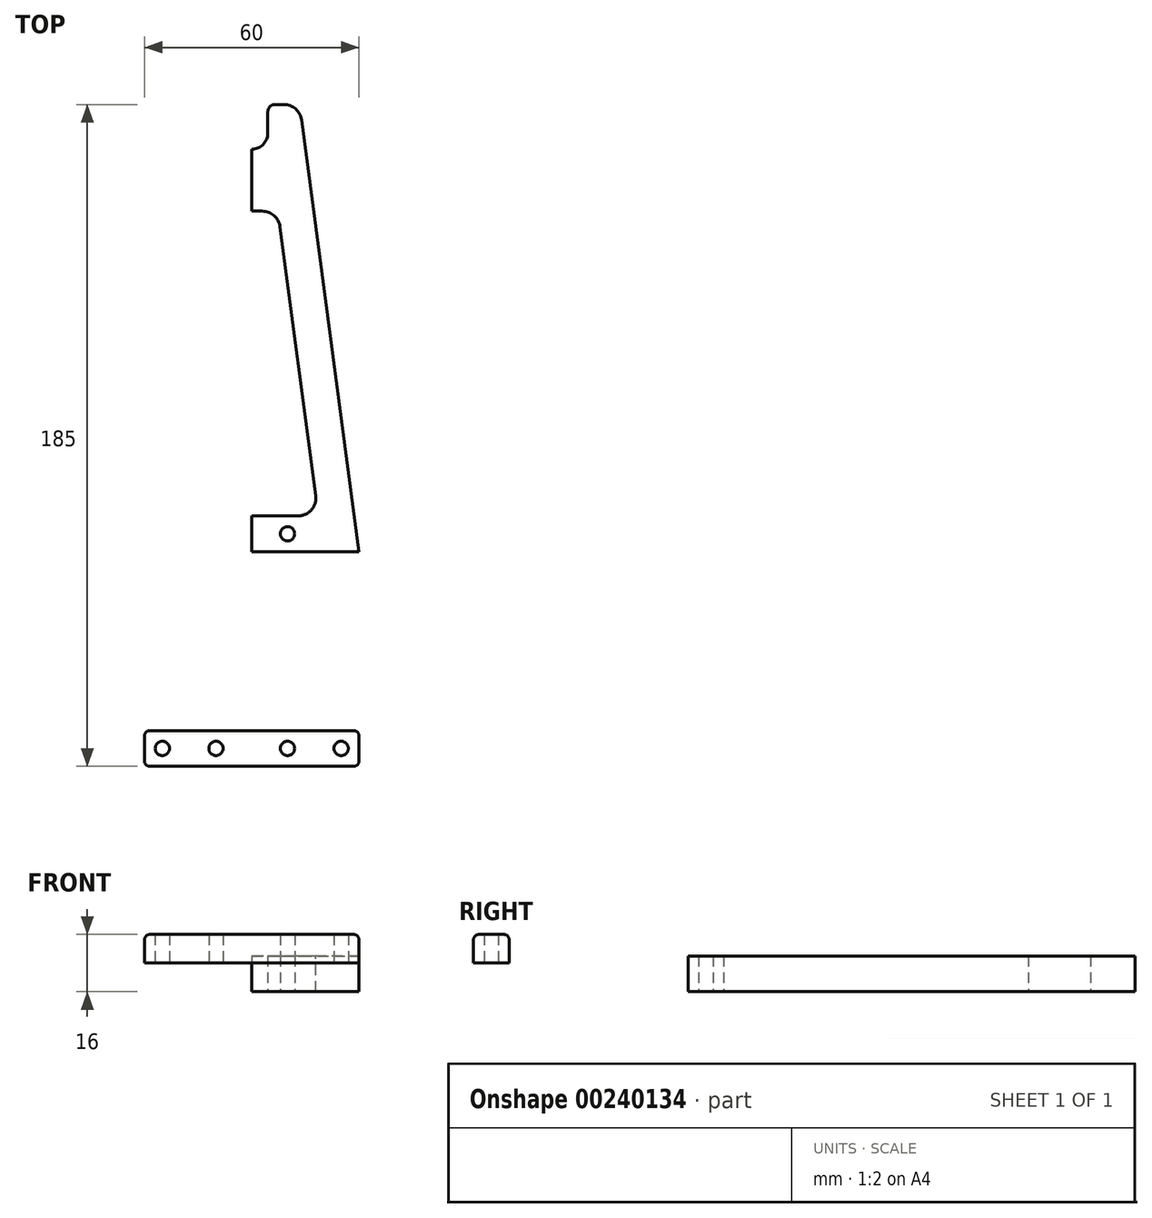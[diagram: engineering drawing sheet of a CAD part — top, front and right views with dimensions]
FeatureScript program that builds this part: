
annotation { "Feature Type Name" : "Feature", "Feature Type Description" : "" }
export const myFeature = defineFeature(function(context is Context, id is Id, definition is map)
    precondition{}
    {
        {
            var Q0;
            Q0=qCreatedBy(makeId("Top.planeOp"),FACE);
            var sketch = newSketch(context, id + "F0", { "sketchPlane" : qUnion([Q0])});
            skLineSegment(sketch, "E0.top", {"start": v(0, 75) * mm, "end": v(-30, 75) * mm});
            skPoint(sketch, "E0.middle", {"position": v(0, 0) * mm});
            skLineSegment(sketch, "E1", {"start": v(-30, 75) * mm, "end": v(-50, -75) * mm});
            skPoint(sketch, "E0.right.end.orphan", {"position": v(-50, 75) * mm});
            skPoint(sketch, "E0.left.end.orphan", {"position": v(50, 75) * mm});
            skLineSegment(sketch, "E2", {"start": v(0, 0) * mm, "end": v(0, 6) * mm});
            skLineSegment(sketch, "E3", {"start": v(-50, -75) * mm, "end": v(-40, -75) * mm});
            skLineSegment(sketch, "E4", {"start": v(-30, 75) * mm, "end": v(-20, 75) * mm});
            skLineSegment(sketch, "E5", {"start": v(0, 75) * mm, "end": v(0, 65) * mm});
            skLineSegment(sketch, "E6", {"start": v(0, 65) * mm, "end": v(-21.33, 65) * mm});
            skLineSegment(sketch, "E7", {"start": v(0, -75) * mm, "end": v(0, -65) * mm});
            skLineSegment(sketch, "E8", {"start": v(0, -65) * mm, "end": v(-38.67, -65) * mm});
            skLineSegment(sketch, "E9", {"start": v(0, 6) * mm, "end": v(-29.2, 6) * mm});
            skLineSegment(sketch, "E10", {"start": v(0, 0) * mm, "end": v(0, -6) * mm});
            skLineSegment(sketch, "E11", {"start": v(0, -6) * mm, "end": v(-30.8, -6) * mm});
            skLineSegment(sketch, "E12.trimOffspring", {"start": v(-30.8, -6) * mm, "end": v(-38.67, -65) * mm});
            skLineSegment(sketch, "E13", {"start": v(-21.33, 65) * mm, "end": v(-29.2, 6) * mm});
            skLineSegment(sketch, "E14.trimOffspring", {"start": v(0, -75) * mm, "end": v(-50, -75) * mm});
            skPoint(sketch, "E0.bottom.start.orphan", {"position": v(50, -75) * mm});
            skCircle(sketch, "E15", {"center": v(-15, 0) * mm, "radius": 2 * mm});
            skLineSegment(sketch, "E16", {"start": v(0, 65) * mm, "end": v(0, 70) * mm});
            skCircle(sketch, "E17", {"center": v(-10.41, 70) * mm, "radius": 2 * mm});
            skSolve(sketch);
        }
        {
            var Q0;
            Q0=qSketchRegion(id+"F0",true);
            extrude(context, id + "F1", {"entities" : qUnion([Q0]), "depth" : 10 * mm});
        }
        {
            var Q0;
            Q0=makeQuery(id+"F1.opExtrude","SWEPT_EDGE",EDGE,{"disambiguationData":[OSD([sQuery(id+"F0.wireOp",EDGE,"E6"),sQuery(id+"F0.wireOp",EDGE,"E13")])]});
            var Q1;
            Q1=makeQuery(id+"F1.opExtrude","SWEPT_EDGE",EDGE,{"disambiguationData":[OSD([sQuery(id+"F0.wireOp",EDGE,"E11"),sQuery(id+"F0.wireOp",EDGE,"E12.trimOffspring")])]});
            var Q2;
            Q2=makeQuery(id+"F1.opExtrude","SWEPT_EDGE",EDGE,{"disambiguationData":[OSD([sQuery(id+"F0.wireOp",EDGE,"E9"),sQuery(id+"F0.wireOp",EDGE,"E13")])]});
            var Q3;
            Q3=makeQuery(id+"F1.opExtrude","SWEPT_EDGE",EDGE,{"disambiguationData":[OSD([sQuery(id+"F0.wireOp",EDGE,"E8"),sQuery(id+"F0.wireOp",EDGE,"E12.trimOffspring")])]});
            var Q4;
            Q4=makeQuery(id+"F1.opExtrude","SWEPT_EDGE",EDGE,{"disambiguationData":[OSD([sQuery(id+"F0.wireOp",EDGE,"E1"),sQuery(id+"F0.wireOp",EDGE,"E14.trimOffspring")])]});
            fillet(context, id + "F2", {"entities" : qUnion([Q0, Q1, Q2, Q3, Q4]), "radius" : 5 * mm, "tangentPropagation" : true, "allowEdgeOverflow" : false});
        }
        {
            var Q0;
            Q0=makeQuery(id+"F1.opExtrude","SWEPT_BODY",BODY,{"disambiguationData":[OSD([sQuery(id+"F0.wireOp",EDGE,"E0.top"),sQuery(id+"F0.wireOp",EDGE,"E1"),sQuery(id+"F0.wireOp",EDGE,"E2"),sQuery(id+"F0.wireOp",EDGE,"E4"),sQuery(id+"F0.wireOp",EDGE,"E5"),sQuery(id+"F0.wireOp",EDGE,"E6"),sQuery(id+"F0.wireOp",EDGE,"E7"),sQuery(id+"F0.wireOp",EDGE,"E8"),sQuery(id+"F0.wireOp",EDGE,"E9"),sQuery(id+"F0.wireOp",EDGE,"E10"),sQuery(id+"F0.wireOp",EDGE,"E11"),sQuery(id+"F0.wireOp",EDGE,"E12.trimOffspring"),sQuery(id+"F0.wireOp",EDGE,"E13"),sQuery(id+"F0.wireOp",EDGE,"E14.trimOffspring"),sQuery(id+"F0.wireOp",EDGE,"E15"),sQuery(id+"F0.wireOp",EDGE,"E16"),sQuery(id+"F0.wireOp",EDGE,"E17")])]});
            var Q1;
            Q1=qCreatedBy(makeId("Right.planeOp"),FACE);
            mirror(context, id + "F3", {"operationType" : NewBodyOperationType.ADD, "entities" : qUnion([Q0]), "mirrorPlane" : qUnion([Q1])});
        }
        {
            var Q0;
            Q0=qCreatedBy(makeId("Top.planeOp"),FACE);
            var sketch = newSketch(context, id + "F4", { "sketchPlane" : qUnion([Q0])});
            skLineSegment(sketch, "E18", {"start": v(0, 0) * mm, "end": v(40, 0) * mm});
            skLineSegment(sketch, "E19", {"start": v(0, 75) * mm, "end": v(30, 75) * mm});
            skLineSegment(sketch, "E20", {"start": v(0, 75) * mm, "end": v(0, 85) * mm});
            skLineSegment(sketch, "E21", {"start": v(4.5, 200) * mm, "end": v(13.33, 200) * mm});
            skLineSegment(sketch, "E22", {"start": v(30, 75) * mm, "end": v(13.33, 200) * mm});
            skArc(sketch, "E23", {"start": v(0, 187.5) * mm, "mid": v(3.18, 188.82) * mm, "end": v(4.5, 192) * mm});
            skLineSegment(sketch, "E24", {"start": v(4.5, 200) * mm, "end": v(4.5, 192) * mm});
            skLineSegment(sketch, "E25", {"start": v(0, 75) * mm, "end": v(0, 80) * mm});
            skCircle(sketch, "E26", {"center": v(10, 80) * mm, "radius": 2 * mm});
            skLineSegment(sketch, "E27", {"start": v(0, 75) * mm, "end": v(10, 75) * mm});
            skLineSegment(sketch, "E28", {"start": v(10, 85) * mm, "end": v(18.67, 85) * mm});
            skLineSegment(sketch, "E29", {"start": v(18.67, 85) * mm, "end": v(10, 150) * mm});
            skLineSegment(sketch, "E30", {"start": v(10, 85) * mm, "end": v(0, 85) * mm});
            skLineSegment(sketch, "E31", {"start": v(18.67, 85) * mm, "end": v(7.31, 170.17) * mm});
            skLineSegment(sketch, "E32", {"start": v(7.31, 170.17) * mm, "end": v(0, 170.17) * mm});
            skLineSegment(sketch, "E33.trimOffspring", {"start": v(0, 170.17) * mm, "end": v(0, 187.5) * mm});
            skSolve(sketch);
        }
        {
            var Q0;
            Q0=qSketchRegion(id+"F4",true);
            extrude(context, id + "F5", {"entities" : qUnion([Q0]), "depth" : 10 * mm});
        }
        {
            var Q0;
            Q0=makeQuery(id+"F5.opExtrude","SWEPT_BODY",BODY,{"disambiguationData":[OSD([sQuery(id+"F4.wireOp",EDGE,"E19"),sQuery(id+"F4.wireOp",EDGE,"E20"),sQuery(id+"F4.wireOp",EDGE,"E21"),sQuery(id+"F4.wireOp",EDGE,"E22"),sQuery(id+"F4.wireOp",EDGE,"E23"),sQuery(id+"F4.wireOp",EDGE,"E24"),sQuery(id+"F4.wireOp",EDGE,"E25"),sQuery(id+"F4.wireOp",EDGE,"E26"),sQuery(id+"F4.wireOp",EDGE,"E27"),sQuery(id+"F4.wireOp",EDGE,"E28"),sQuery(id+"F4.wireOp",EDGE,"E30"),sQuery(id+"F4.wireOp",EDGE,"E31"),sQuery(id+"F4.wireOp",EDGE,"E32"),sQuery(id+"F4.wireOp",EDGE,"E33.trimOffspring")])]});
            var Q1;
            Q1=qCreatedBy(makeId("Right.planeOp"),FACE);
            mirror(context, id + "F6", {"entities" : qUnion([Q0]), "mirrorPlane" : qUnion([Q1])});
        }
        {
            var Q0;
            Q0=makeQuery(id+"F6.opPattern","COPY",EDGE,{"derivedFrom":makeQuery(id+"F5.opExtrude","SWEPT_EDGE",EDGE,{"disambiguationData":[OSD([sQuery(id+"F4.wireOp",EDGE,"E31"),sQuery(id+"F4.wireOp",EDGE,"E32")])]}),"instanceName":"1"});
            var Q1;
            Q1=makeQuery(id+"F5.opExtrude","SWEPT_EDGE",EDGE,{"disambiguationData":[OSD([sQuery(id+"F4.wireOp",EDGE,"E31"),sQuery(id+"F4.wireOp",EDGE,"E32")])]});
            var Q2;
            Q2=makeQuery(id+"F6.opPattern","COPY",EDGE,{"derivedFrom":makeQuery(id+"F5.opExtrude","SWEPT_EDGE",EDGE,{"disambiguationData":[OSD([sQuery(id+"F4.wireOp",EDGE,"E28"),sQuery(id+"F4.wireOp",EDGE,"E31")])]}),"instanceName":"1"});
            var Q3;
            Q3=makeQuery(id+"F5.opExtrude","SWEPT_EDGE",EDGE,{"disambiguationData":[OSD([sQuery(id+"F4.wireOp",EDGE,"E28"),sQuery(id+"F4.wireOp",EDGE,"E31")])]});
            var Q4;
            Q4=makeQuery(id+"F6.opPattern","COPY",EDGE,{"derivedFrom":makeQuery(id+"F5.opExtrude","SWEPT_EDGE",EDGE,{"disambiguationData":[OSD([sQuery(id+"F4.wireOp",EDGE,"E21"),sQuery(id+"F4.wireOp",EDGE,"E22")])]}),"instanceName":"1"});
            var Q5;
            Q5=makeQuery(id+"F5.opExtrude","SWEPT_EDGE",EDGE,{"disambiguationData":[OSD([sQuery(id+"F4.wireOp",EDGE,"E21"),sQuery(id+"F4.wireOp",EDGE,"E22")])]});
            fillet(context, id + "F7", {"entities" : qUnion([Q0, Q1, Q2, Q3, Q4, Q5]), "radius" : 5 * mm, "tangentPropagation" : true, "allowEdgeOverflow" : false});
        }
        {
            var Q0;
            Q0=makeQuery(id+"F5.opExtrude","SWEPT_EDGE",EDGE,{"disambiguationData":[OSD([sQuery(id+"F4.wireOp",EDGE,"E21"),sQuery(id+"F4.wireOp",EDGE,"E24")])]});
            var Q1;
            Q1=makeQuery(id+"F6.opPattern","COPY",EDGE,{"derivedFrom":makeQuery(id+"F5.opExtrude","SWEPT_EDGE",EDGE,{"disambiguationData":[OSD([sQuery(id+"F4.wireOp",EDGE,"E21"),sQuery(id+"F4.wireOp",EDGE,"E24")])]}),"instanceName":"1"});
            fillet(context, id + "F8", {"entities" : qUnion([Q0, Q1]), "radius" : 2 * mm, "tangentPropagation" : true, "allowEdgeOverflow" : false});
        }
        {
            var Q0;
            Q0=qCreatedBy(makeId("Top.planeOp"),FACE);
            var sketch = newSketch(context, id + "F9", { "sketchPlane" : qUnion([Q0])});
            skLineSegment(sketch, "E34", {"start": v(0, 0) * mm, "end": v(0, 6) * mm});
            skLineSegment(sketch, "E35", {"start": v(0, 6) * mm, "end": v(-6, 6) * mm});
            skLineSegment(sketch, "E36", {"start": v(-6, 6) * mm, "end": v(-6, -6) * mm});
            skLineSegment(sketch, "E37", {"start": v(-6, -6) * mm, "end": v(0, -6) * mm});
            skLineSegment(sketch, "E38", {"start": v(0, -6) * mm, "end": v(0, 0) * mm});
            skSolve(sketch);
        }
        {
            var Q0;
            Q0=qSketchRegion(id+"F9",true);
            extrude(context, id + "F10", {"entities" : qUnion([Q0]), "operationType" : NewBodyOperationType.ADD, "depth" : 25 * mm});
        }
        {
            var Q0;
            Q0=makeQuery(id+"F10.opExtrude","SWEPT_EDGE",EDGE,{"disambiguationData":[OSD([sQuery(id+"F9.wireOp",EDGE,"E36"),sQuery(id+"F9.wireOp",EDGE,"E37")])]});
            var Q1;
            Q1=makeQuery(id+"F10.opExtrude","CAP_EDGE",EDGE,{"disambiguationData":[OSD([sQuery(id+"F9.wireOp",EDGE,"E36")])],"isStart":false});
            var Q2;
            Q2=makeQuery(id+"F10.opExtrude","CAP_EDGE",EDGE,{"disambiguationData":[OSD([sQuery(id+"F9.wireOp",EDGE,"E37")])],"isStart":false});
            var Q3;
            Q3=makeQuery(id+"F10.opExtrude","SWEPT_EDGE",EDGE,{"disambiguationData":[OSD([sQuery(id+"F9.wireOp",EDGE,"E35"),sQuery(id+"F9.wireOp",EDGE,"E36")])]});
            var Q4;
            Q4=makeQuery(id+"F10.opExtrude","CAP_EDGE",EDGE,{"disambiguationData":[OSD([sQuery(id+"F9.wireOp",EDGE,"E35")])],"isStart":false});
            fillet(context, id + "F11", {"entities" : qUnion([Q0, Q1, Q2, Q3, Q4]), "radius" : 1.5 * mm, "tangentPropagation" : true, "allowEdgeOverflow" : false});
        }
        {
            var Q0;
            Q0=qCreatedBy(makeId("Right.planeOp"),FACE);
            var sketch = newSketch(context, id + "F12", { "sketchPlane" : qUnion([Q0])});
            skCircle(sketch, "E39", {"center": v(0, 20) * mm, "radius": 1.75 * mm});
            skCircle(sketch, "E40", {"center": v(0, 15) * mm, "radius": 1.75 * mm});
            skSolve(sketch);
        }
        {
            var Q0;
            Q0=qSketchRegion(id+"F12",true);
            extrude(context, id + "F13", {"entities" : qUnion([Q0]), "endBound" : BoundingType.SYMMETRIC, "depth" : 25 * mm});
        }
        {
            var Q0;
            Q0=makeQuery(id+"F13.opExtrude","SWEPT_BODY",BODY,{"disambiguationData":[OSD([sQuery(id+"F12.wireOp",EDGE,"E40")])]});
            var Q1;
            Q1=makeQuery(id+"F13.opExtrude","SWEPT_BODY",BODY,{"disambiguationData":[OSD([sQuery(id+"F12.wireOp",EDGE,"E39")])]});
            var Q2;
            Q2=makeQuery(id+"F1.opExtrude","SWEPT_BODY",BODY,{"disambiguationData":[OSD([sQuery(id+"F0.wireOp",EDGE,"E0.top"),sQuery(id+"F0.wireOp",EDGE,"E1"),sQuery(id+"F0.wireOp",EDGE,"E2"),sQuery(id+"F0.wireOp",EDGE,"E4"),sQuery(id+"F0.wireOp",EDGE,"E5"),sQuery(id+"F0.wireOp",EDGE,"E6"),sQuery(id+"F0.wireOp",EDGE,"E7"),sQuery(id+"F0.wireOp",EDGE,"E8"),sQuery(id+"F0.wireOp",EDGE,"E9"),sQuery(id+"F0.wireOp",EDGE,"E10"),sQuery(id+"F0.wireOp",EDGE,"E11"),sQuery(id+"F0.wireOp",EDGE,"E12.trimOffspring"),sQuery(id+"F0.wireOp",EDGE,"E13"),sQuery(id+"F0.wireOp",EDGE,"E14.trimOffspring"),sQuery(id+"F0.wireOp",EDGE,"E15"),sQuery(id+"F0.wireOp",EDGE,"E16"),sQuery(id+"F0.wireOp",EDGE,"E17")])]});
            booleanBodies(context, id + "F14", {"operationType" : BooleanOperationType.SUBTRACTION, "tools" : qUnion([Q0, Q1]), "targets" : qUnion([Q2])});
        }
        {
            var Q0;
            Q0=qCreatedBy(makeId("Top.planeOp"),FACE);
            var sketch = newSketch(context, id + "F15", { "sketchPlane" : qUnion([Q0])});
            skLineSegment(sketch, "E41.bottom", {"start": v(15, 65) * mm, "end": v(-15, 65) * mm});
            skLineSegment(sketch, "E41.top", {"start": v(15, 85) * mm, "end": v(-15, 85) * mm});
            skLineSegment(sketch, "E41.left", {"start": v(15, 65) * mm, "end": v(15, 85) * mm});
            skLineSegment(sketch, "E41.right", {"start": v(-15, 65) * mm, "end": v(-15, 85) * mm});
            skPoint(sketch, "E41.middle", {"position": v(0, 75) * mm});
            skLineSegment(sketch, "E42", {"start": v(0, 75) * mm, "end": v(0, 85) * mm});
            skLineSegment(sketch, "E43", {"start": v(0, 85) * mm, "end": v(0, 65) * mm});
            skLineSegment(sketch, "E44", {"start": v(0, 65) * mm, "end": v(-6, 65) * mm});
            skLineSegment(sketch, "E45", {"start": v(-6, 65) * mm, "end": v(-6, 85) * mm});
            skLineSegment(sketch, "E46", {"start": v(-6, 85) * mm, "end": v(0, 85) * mm});
            skSolve(sketch);
        }
        {
            var Q0;
            Q0=qSketchRegion(id+"F15",true);
            extrude(context, id + "F16", {"entities" : qUnion([Q0]), "depth" : 10 * mm});
        }
        {
            var Q0;
            Q0=qCreatedBy(makeId("Top.planeOp"),FACE);
            var sketch = newSketch(context, id + "F17", { "sketchPlane" : qUnion([Q0])});
            skLineSegment(sketch, "E47", {"start": v(0, 65) * mm, "end": v(0, 85) * mm});
            skLineSegment(sketch, "E48", {"start": v(0, 85) * mm, "end": v(-6, 85) * mm});
            skLineSegment(sketch, "E49", {"start": v(-6, 85) * mm, "end": v(-6, 65) * mm});
            skLineSegment(sketch, "E50", {"start": v(-6, 65) * mm, "end": v(0, 65) * mm});
            skSolve(sketch);
        }
        {
            var Q0;
            Q0=qSketchRegion(id+"F17",true);
            extrude(context, id + "F18", {"entities" : qUnion([Q0]), "depth" : 25 * mm});
        }
        {
            var Q0;
            Q0=makeQuery(id+"F16.opExtrude","SWEPT_BODY",BODY,{"disambiguationData":[OSD([sQuery(id+"F15.wireOp",EDGE,"E41.bottom"),sQuery(id+"F15.wireOp",EDGE,"E41.top"),sQuery(id+"F15.wireOp",EDGE,"E41.left"),sQuery(id+"F15.wireOp",EDGE,"E41.right"),sQuery(id+"F15.wireOp",EDGE,"E44"),sQuery(id+"F15.wireOp",EDGE,"E46")])]});
            var Q1;
            Q1=makeQuery(id+"F18.opExtrude","SWEPT_BODY",BODY,{"disambiguationData":[OSD([sQuery(id+"F17.wireOp",EDGE,"E47"),sQuery(id+"F17.wireOp",EDGE,"E48"),sQuery(id+"F17.wireOp",EDGE,"E49"),sQuery(id+"F17.wireOp",EDGE,"E50")])]});
            booleanBodies(context, id + "F19", {"operationType" : BooleanOperationType.UNION, "tools" : qUnion([Q0, Q1])});
        }
        {
            var Q0;
            Q0=makeQuery(id+"F16.opExtrude","SWEPT_BODY",BODY,{"disambiguationData":[OSD([sQuery(id+"F15.wireOp",EDGE,"E41.bottom"),sQuery(id+"F15.wireOp",EDGE,"E41.top"),sQuery(id+"F15.wireOp",EDGE,"E41.left"),sQuery(id+"F15.wireOp",EDGE,"E41.right"),sQuery(id+"F15.wireOp",EDGE,"E44"),sQuery(id+"F15.wireOp",EDGE,"E46")])]});
            transform(context, id + "F20", {"entities" : qUnion([Q0]), "transformType" : TransformType.TRANSLATION_3D, "dx" : 0 * mm, "dy" : 0 * mm, "dz" : 10 * mm, "makeCopy" : false});
        }
        {
            var Q0;
            Q0=qCreatedBy(makeId("Top.planeOp"),FACE);
            var sketch = newSketch(context, id + "F21", { "sketchPlane" : qUnion([Q0])});
            skCircle(sketch, "E51", {"center": v(-10, 80) * mm, "radius": 2 * mm});
            skCircle(sketch, "E52", {"center": v(10, 80) * mm, "radius": 2 * mm});
            skCircle(sketch, "E53", {"center": v(-10.4, 70) * mm, "radius": 2 * mm});
            skCircle(sketch, "E54", {"center": v(10.4, 70) * mm, "radius": 2 * mm});
            skSolve(sketch);
        }
        {
            var Q0;
            Q0=qSketchRegion(id+"F21",true);
            extrude(context, id + "F22", {"entities" : qUnion([Q0]), "depth" : 30 * mm});
        }
        {
            var Q0;
            Q0=makeQuery(id+"F22.opExtrude","SWEPT_BODY",BODY,{"disambiguationData":[OSD([sQuery(id+"F21.wireOp",EDGE,"E54")])]});
            var Q1;
            Q1=makeQuery(id+"F22.opExtrude","SWEPT_BODY",BODY,{"disambiguationData":[OSD([sQuery(id+"F21.wireOp",EDGE,"E53")])]});
            var Q2;
            Q2=makeQuery(id+"F22.opExtrude","SWEPT_BODY",BODY,{"disambiguationData":[OSD([sQuery(id+"F21.wireOp",EDGE,"E52")])]});
            var Q3;
            Q3=makeQuery(id+"F22.opExtrude","SWEPT_BODY",BODY,{"disambiguationData":[OSD([sQuery(id+"F21.wireOp",EDGE,"E51")])]});
            var Q4;
            Q4=makeQuery(id+"F16.opExtrude","SWEPT_BODY",BODY,{"disambiguationData":[OSD([sQuery(id+"F15.wireOp",EDGE,"E41.bottom"),sQuery(id+"F15.wireOp",EDGE,"E41.top"),sQuery(id+"F15.wireOp",EDGE,"E41.left"),sQuery(id+"F15.wireOp",EDGE,"E41.right"),sQuery(id+"F15.wireOp",EDGE,"E44"),sQuery(id+"F15.wireOp",EDGE,"E46")])]});
            booleanBodies(context, id + "F23", {"operationType" : BooleanOperationType.SUBTRACTION, "tools" : qUnion([Q0, Q1, Q2, Q3]), "targets" : qUnion([Q4])});
        }
        {
            var Q0;
            Q0=qCreatedBy(makeId("Right.planeOp"),FACE);
            var sketch = newSketch(context, id + "F24", { "sketchPlane" : qUnion([Q0])});
            skCircle(sketch, "E55", {"center": v(80, 27.23) * mm, "radius": 2 * mm});
            skCircle(sketch, "E56", {"center": v(70, 27.23) * mm, "radius": 2 * mm});
            skSolve(sketch);
        }
        {
            var Q0;
            Q0=qSketchRegion(id+"F24",true);
            extrude(context, id + "F25", {"entities" : qUnion([Q0]), "endBound" : BoundingType.SYMMETRIC, "depth" : 25 * mm});
        }
        {
            var Q0;
            Q0=makeQuery(id+"F25.opExtrude","SWEPT_BODY",BODY,{"disambiguationData":[OSD([sQuery(id+"F24.wireOp",EDGE,"E56")])]});
            var Q1;
            Q1=makeQuery(id+"F25.opExtrude","SWEPT_BODY",BODY,{"disambiguationData":[OSD([sQuery(id+"F24.wireOp",EDGE,"E55")])]});
            var Q2;
            Q2=makeQuery(id+"F16.opExtrude","SWEPT_BODY",BODY,{"disambiguationData":[OSD([sQuery(id+"F15.wireOp",EDGE,"E41.bottom"),sQuery(id+"F15.wireOp",EDGE,"E41.top"),sQuery(id+"F15.wireOp",EDGE,"E41.left"),sQuery(id+"F15.wireOp",EDGE,"E41.right"),sQuery(id+"F15.wireOp",EDGE,"E44"),sQuery(id+"F15.wireOp",EDGE,"E46")])]});
            booleanBodies(context, id + "F26", {"operationType" : BooleanOperationType.SUBTRACTION, "tools" : qUnion([Q0, Q1]), "targets" : qUnion([Q2])});
        }
        {
            var Q0;
            Q0=makeQuery(id+"F18.opExtrude","SWEPT_EDGE",EDGE,{"disambiguationData":[OSD([sQuery(id+"F17.wireOp",EDGE,"E49"),sQuery(id+"F17.wireOp",EDGE,"E50")])]});
            var Q1;
            Q1=makeQuery(id+"F18.opExtrude","CAP_EDGE",EDGE,{"disambiguationData":[OSD([sQuery(id+"F17.wireOp",EDGE,"E50")])],"isStart":false});
            var Q2;
            {var subQ0=sQuery(id+"F15.wireOp",EDGE,"E44");var subQ1=sQuery(id+"F15.wireOp",EDGE,"E41.bottom");var subQ2=sQuery(id+"F15.wireOp",EDGE,"E41.right");Q2=makeQuery(id+"F19.opBoolean","SPLIT",EDGE,{"disambiguationData":[TD([makeQuery(id+"F16.opExtrude","SWEPT_FACE",FACE,{"disambiguationData":[OSD([subQ2])]})])],"derivedFrom":makeQuery(id+"F16.opExtrude","CAP_EDGE",EDGE,{"disambiguationData":[OSD([subQ1,subQ0])],"isStart":false})});}
            var Q3;
            Q3=makeQuery(id+"F16.opExtrude","SWEPT_EDGE",EDGE,{"disambiguationData":[OSD([sQuery(id+"F15.wireOp",EDGE,"E41.bottom"),sQuery(id+"F15.wireOp",EDGE,"E41.right")])]});
            var Q4;
            {var subQ0=sQuery(id+"F15.wireOp",EDGE,"E41.left");var subQ1=sQuery(id+"F15.wireOp",EDGE,"E44");var subQ2=sQuery(id+"F15.wireOp",EDGE,"E41.bottom");Q4=makeQuery(id+"F19.opBoolean","SPLIT",EDGE,{"disambiguationData":[TD([makeQuery(id+"F16.opExtrude","SWEPT_FACE",FACE,{"disambiguationData":[OSD([subQ0])]})])],"derivedFrom":makeQuery(id+"F16.opExtrude","CAP_EDGE",EDGE,{"disambiguationData":[OSD([subQ2,subQ1])],"isStart":false})});}
            var Q5;
            Q5=makeQuery(id+"F16.opExtrude","SWEPT_EDGE",EDGE,{"disambiguationData":[OSD([sQuery(id+"F15.wireOp",EDGE,"E41.bottom"),sQuery(id+"F15.wireOp",EDGE,"E41.left")])]});
            var Q6;
            Q6=makeQuery(id+"F16.opExtrude","CAP_EDGE",EDGE,{"disambiguationData":[OSD([sQuery(id+"F15.wireOp",EDGE,"E41.left")])],"isStart":false});
            var Q7;
            Q7=makeQuery(id+"F16.opExtrude","CAP_EDGE",EDGE,{"disambiguationData":[OSD([sQuery(id+"F15.wireOp",EDGE,"E41.right")])],"isStart":false});
            var Q8;
            Q8=makeQuery(id+"F18.opExtrude","CAP_EDGE",EDGE,{"disambiguationData":[OSD([sQuery(id+"F17.wireOp",EDGE,"E49")])],"isStart":false});
            var Q9;
            {var subQ0=sQuery(id+"F15.wireOp",EDGE,"E41.right");var subQ1=sQuery(id+"F15.wireOp",EDGE,"E46");var subQ2=sQuery(id+"F15.wireOp",EDGE,"E41.top");Q9=makeQuery(id+"F19.opBoolean","SPLIT",EDGE,{"disambiguationData":[TD([makeQuery(id+"F16.opExtrude","SWEPT_FACE",FACE,{"disambiguationData":[OSD([subQ0])]})])],"derivedFrom":makeQuery(id+"F16.opExtrude","CAP_EDGE",EDGE,{"disambiguationData":[OSD([subQ2,subQ1])],"isStart":false})});}
            var Q10;
            Q10=makeQuery(id+"F16.opExtrude","SWEPT_EDGE",EDGE,{"disambiguationData":[OSD([sQuery(id+"F15.wireOp",EDGE,"E41.top"),sQuery(id+"F15.wireOp",EDGE,"E41.right")])]});
            var Q11;
            Q11=makeQuery(id+"F18.opExtrude","SWEPT_EDGE",EDGE,{"disambiguationData":[OSD([sQuery(id+"F17.wireOp",EDGE,"E48"),sQuery(id+"F17.wireOp",EDGE,"E49")])]});
            var Q12;
            Q12=makeQuery(id+"F18.opExtrude","CAP_EDGE",EDGE,{"disambiguationData":[OSD([sQuery(id+"F17.wireOp",EDGE,"E48")])],"isStart":false});
            var Q13;
            {var subQ0=sQuery(id+"F15.wireOp",EDGE,"E41.left");var subQ1=sQuery(id+"F15.wireOp",EDGE,"E46");var subQ2=sQuery(id+"F15.wireOp",EDGE,"E41.top");Q13=makeQuery(id+"F19.opBoolean","SPLIT",EDGE,{"disambiguationData":[TD([makeQuery(id+"F16.opExtrude","SWEPT_FACE",FACE,{"disambiguationData":[OSD([subQ0])]})])],"derivedFrom":makeQuery(id+"F16.opExtrude","CAP_EDGE",EDGE,{"disambiguationData":[OSD([subQ2,subQ1])],"isStart":false})});}
            var Q14;
            Q14=makeQuery(id+"F16.opExtrude","SWEPT_EDGE",EDGE,{"disambiguationData":[OSD([sQuery(id+"F15.wireOp",EDGE,"E41.top"),sQuery(id+"F15.wireOp",EDGE,"E41.left")])]});
            fillet(context, id + "F27", {"entities" : qUnion([Q0, Q1, Q2, Q3, Q4, Q5, Q6, Q7, Q8, Q9, Q10, Q11, Q12, Q13, Q14]), "radius" : 2 * mm, "tangentPropagation" : true, "allowEdgeOverflow" : false});
        }
        {
            var Q0;
            Q0=qCreatedBy(makeId("Right.planeOp"),FACE);
            var sketch = newSketch(context, id + "F28", { "sketchPlane" : qUnion([Q0])});
            skLineSegment(sketch, "E57", {"start": v(0, 0) * mm, "end": v(0, 10) * mm});
            skLineSegment(sketch, "E58", {"start": v(0, 10) * mm, "end": v(6, 10) * mm});
            skLineSegment(sketch, "E59", {"start": v(6, 10) * mm, "end": v(6, 25) * mm});
            skLineSegment(sketch, "E60", {"start": v(-6, 25) * mm, "end": v(-6, 10) * mm});
            skLineSegment(sketch, "E61", {"start": v(-6, 10) * mm, "end": v(0, 10) * mm});
            skLineSegment(sketch, "E62", {"start": v(75, 10) * mm, "end": v(75, 20) * mm});
            skLineSegment(sketch, "E63", {"start": v(75, 20) * mm, "end": v(85, 20) * mm});
            skLineSegment(sketch, "E64", {"start": v(85, 20) * mm, "end": v(85, 35) * mm});
            skLineSegment(sketch, "E65", {"start": v(65, 35) * mm, "end": v(65, 20) * mm});
            skLineSegment(sketch, "E66", {"start": v(65, 20) * mm, "end": v(75, 20) * mm});
            skLineSegment(sketch, "E67", {"start": v(-6, 10) * mm, "end": v(-6, 25) * mm});
            skLineSegment(sketch, "E68", {"start": v(75, 120) * mm, "end": v(85, 120) * mm});
            skLineSegment(sketch, "E69", {"start": v(85, 35) * mm, "end": v(85, 120) * mm});
            skLineSegment(sketch, "E70", {"start": v(85, 120) * mm, "end": v(75, 120) * mm});
            skLineSegment(sketch, "E71", {"start": v(6, 25) * mm, "end": v(65, 35) * mm});
            skLineSegment(sketch, "E72", {"start": v(-6, 25) * mm, "end": v(75, 120) * mm});
            skLineSegment(sketch, "E73", {"start": v(23.92, 44.68) * mm, "end": v(75, 104.59) * mm});
            skLineSegment(sketch, "E74", {"start": v(23.92, 44.68) * mm, "end": v(17.44, 37.08) * mm});
            skLineSegment(sketch, "E75", {"start": v(75, 45) * mm, "end": v(64.16, 45) * mm});
            skLineSegment(sketch, "E76", {"start": v(51.92, 42.93) * mm, "end": v(17.44, 37.08) * mm});
            skLineSegment(sketch, "E77", {"start": v(51.92, 42.93) * mm, "end": v(64.16, 45) * mm});
            skPoint(sketch, "E78.orphan", {"position": v(75, 35) * mm});
            skPoint(sketch, "E79.start.orphan", {"position": v(75, 110) * mm});
            skLineSegment(sketch, "E80", {"start": v(75, 104.59) * mm, "end": v(75, 45) * mm});
            skCircle(sketch, "E81", {"center": v(80, 110) * mm, "radius": 2 * mm});
            skCircle(sketch, "E82", {"center": v(80, 95) * mm, "radius": 2 * mm});
            skPoint(sketch, "E83.end.orphan", {"position": v(80, 120) * mm});
            skSolve(sketch);
        }
        {
            var Q0;
            Q0=qSketchRegion(id+"F28",true);
            extrude(context, id + "F29", {"entities" : qUnion([Q0]), "depth" : 8 * mm});
        }
        {
            var Q0;
            Q0=makeQuery(id+"F29.opExtrude","SWEPT_EDGE",EDGE,{"disambiguationData":[OSD([sQuery(id+"F28.wireOp",EDGE,"E73"),sQuery(id+"F28.wireOp",EDGE,"E80")])]});
            var Q1;
            Q1=makeQuery(id+"F29.opExtrude","SWEPT_EDGE",EDGE,{"disambiguationData":[OSD([sQuery(id+"F28.wireOp",EDGE,"E75"),sQuery(id+"F28.wireOp",EDGE,"E80")])]});
            var Q2;
            Q2=makeQuery(id+"F29.opExtrude","SWEPT_EDGE",EDGE,{"disambiguationData":[OSD([sQuery(id+"F28.wireOp",EDGE,"E74"),sQuery(id+"F28.wireOp",EDGE,"E76")])]});
            var Q3;
            Q3=makeQuery(id+"F29.opExtrude","SWEPT_EDGE",EDGE,{"disambiguationData":[OSD([sQuery(id+"F28.wireOp",EDGE,"E65"),sQuery(id+"F28.wireOp",EDGE,"E71")])]});
            var Q4;
            Q4=makeQuery(id+"F29.opExtrude","SWEPT_EDGE",EDGE,{"disambiguationData":[OSD([sQuery(id+"F28.wireOp",EDGE,"E59"),sQuery(id+"F28.wireOp",EDGE,"E71")])]});
            var Q5;
            Q5=makeQuery(id+"F29.opExtrude","SWEPT_EDGE",EDGE,{"disambiguationData":[OSD([sQuery(id+"F28.wireOp",EDGE,"E67"),sQuery(id+"F28.wireOp",EDGE,"E72")])]});
            fillet(context, id + "F30", {"entities" : qUnion([Q0, Q1, Q2, Q3, Q4, Q5]), "radius" : 2 * mm, "tangentPropagation" : true, "allowEdgeOverflow" : false});
        }
        {
            var Q0;
            Q0=makeQuery(id+"F29.opExtrude","CAP_EDGE",EDGE,{"disambiguationData":[OSD([sQuery(id+"F28.wireOp",EDGE,"E73"),sQuery(id+"F28.wireOp",EDGE,"E74")])],"isStart":false});
            var Q1;
            Q1=makeQuery(id+"F29.opExtrude","CAP_EDGE",EDGE,{"disambiguationData":[OSD([sQuery(id+"F28.wireOp",EDGE,"E72")])],"isStart":false});
            var Q2;
            Q2=makeQuery(id+"F29.opExtrude","CAP_EDGE",EDGE,{"disambiguationData":[OSD([sQuery(id+"F28.wireOp",EDGE,"E71")])],"isStart":false});
            var Q3;
            Q3=makeQuery(id+"F29.opExtrude","CAP_EDGE",EDGE,{"disambiguationData":[OSD([sQuery(id+"F28.wireOp",EDGE,"E64"),sQuery(id+"F28.wireOp",EDGE,"E69")])],"isStart":false});
            fillet(context, id + "F31", {"entities" : qUnion([Q0, Q1, Q2, Q3]), "radius" : 2 * mm, "tangentPropagation" : true, "allowEdgeOverflow" : false});
        }
        {
            var Q0;
            Q0=qCreatedBy(makeId("Right.planeOp"),FACE);
            var sketch = newSketch(context, id + "F32", { "sketchPlane" : qUnion([Q0])});
            skCircle(sketch, "E84", {"center": v(0, 20) * mm, "radius": 1.75 * mm});
            skCircle(sketch, "E85", {"center": v(0, 15) * mm, "radius": 1.75 * mm});
            skCircle(sketch, "E86", {"center": v(70, 27.25) * mm, "radius": 2 * mm});
            skCircle(sketch, "E87", {"center": v(80, 27.25) * mm, "radius": 2 * mm});
            skSolve(sketch);
        }
        {
            var Q0;
            Q0=qSketchRegion(id+"F32",true);
            extrude(context, id + "F33", {"entities" : qUnion([Q0]), "depth" : 25 * mm});
        }
        {
            var Q0;
            Q0=makeQuery(id+"F33.opExtrude","SWEPT_BODY",BODY,{"disambiguationData":[OSD([sQuery(id+"F32.wireOp",EDGE,"E87")])]});
            var Q1;
            Q1=makeQuery(id+"F33.opExtrude","SWEPT_BODY",BODY,{"disambiguationData":[OSD([sQuery(id+"F32.wireOp",EDGE,"E86")])]});
            var Q2;
            Q2=makeQuery(id+"F33.opExtrude","SWEPT_BODY",BODY,{"disambiguationData":[OSD([sQuery(id+"F32.wireOp",EDGE,"E85")])]});
            var Q3;
            Q3=makeQuery(id+"F33.opExtrude","SWEPT_BODY",BODY,{"disambiguationData":[OSD([sQuery(id+"F32.wireOp",EDGE,"E84")])]});
            var Q4;
            Q4=makeQuery(id+"F29.opExtrude","SWEPT_BODY",BODY,{"disambiguationData":[OSD([sQuery(id+"F28.wireOp",EDGE,"E59"),sQuery(id+"F28.wireOp",EDGE,"E61"),sQuery(id+"F28.wireOp",EDGE,"E58"),sQuery(id+"F28.wireOp",EDGE,"E63"),sQuery(id+"F28.wireOp",EDGE,"E64"),sQuery(id+"F28.wireOp",EDGE,"E65"),sQuery(id+"F28.wireOp",EDGE,"E66"),sQuery(id+"F28.wireOp",EDGE,"E67"),sQuery(id+"F28.wireOp",EDGE,"E69"),sQuery(id+"F28.wireOp",EDGE,"E70"),sQuery(id+"F28.wireOp",EDGE,"E71"),sQuery(id+"F28.wireOp",EDGE,"E72"),sQuery(id+"F28.wireOp",EDGE,"E73"),sQuery(id+"F28.wireOp",EDGE,"E74"),sQuery(id+"F28.wireOp",EDGE,"E75"),sQuery(id+"F28.wireOp",EDGE,"E76"),sQuery(id+"F28.wireOp",EDGE,"E77"),sQuery(id+"F28.wireOp",EDGE,"E80"),sQuery(id+"F28.wireOp",EDGE,"E81"),sQuery(id+"F28.wireOp",EDGE,"E82")])]});
            booleanBodies(context, id + "F34", {"operationType" : BooleanOperationType.SUBTRACTION, "tools" : qUnion([Q0, Q1, Q2, Q3]), "targets" : qUnion([Q4])});
        }
        {
            var Q0;
            Q0=makeQuery(id+"F16.opExtrude","SWEPT_BODY",BODY,{"disambiguationData":[OSD([sQuery(id+"F15.wireOp",EDGE,"E41.bottom"),sQuery(id+"F15.wireOp",EDGE,"E41.top"),sQuery(id+"F15.wireOp",EDGE,"E41.left"),sQuery(id+"F15.wireOp",EDGE,"E41.right"),sQuery(id+"F15.wireOp",EDGE,"E44"),sQuery(id+"F15.wireOp",EDGE,"E46")])]});
            var Q1;
            Q1=makeQuery(id+"F6.opPattern","COPY",BODY,{"derivedFrom":makeQuery(id+"F5.opExtrude","SWEPT_BODY",BODY,{"disambiguationData":[OSD([sQuery(id+"F4.wireOp",EDGE,"E19"),sQuery(id+"F4.wireOp",EDGE,"E20"),sQuery(id+"F4.wireOp",EDGE,"E21"),sQuery(id+"F4.wireOp",EDGE,"E22"),sQuery(id+"F4.wireOp",EDGE,"E23"),sQuery(id+"F4.wireOp",EDGE,"E24"),sQuery(id+"F4.wireOp",EDGE,"E25"),sQuery(id+"F4.wireOp",EDGE,"E26"),sQuery(id+"F4.wireOp",EDGE,"E27"),sQuery(id+"F4.wireOp",EDGE,"E28"),sQuery(id+"F4.wireOp",EDGE,"E30"),sQuery(id+"F4.wireOp",EDGE,"E31"),sQuery(id+"F4.wireOp",EDGE,"E32"),sQuery(id+"F4.wireOp",EDGE,"E33.trimOffspring")])]}),"instanceName":"1"});
            var Q2;
            Q2=makeQuery(id+"F1.opExtrude","SWEPT_BODY",BODY,{"disambiguationData":[OSD([sQuery(id+"F0.wireOp",EDGE,"E0.top"),sQuery(id+"F0.wireOp",EDGE,"E1"),sQuery(id+"F0.wireOp",EDGE,"E2"),sQuery(id+"F0.wireOp",EDGE,"E4"),sQuery(id+"F0.wireOp",EDGE,"E5"),sQuery(id+"F0.wireOp",EDGE,"E6"),sQuery(id+"F0.wireOp",EDGE,"E7"),sQuery(id+"F0.wireOp",EDGE,"E8"),sQuery(id+"F0.wireOp",EDGE,"E9"),sQuery(id+"F0.wireOp",EDGE,"E10"),sQuery(id+"F0.wireOp",EDGE,"E11"),sQuery(id+"F0.wireOp",EDGE,"E12.trimOffspring"),sQuery(id+"F0.wireOp",EDGE,"E13"),sQuery(id+"F0.wireOp",EDGE,"E14.trimOffspring"),sQuery(id+"F0.wireOp",EDGE,"E15"),sQuery(id+"F0.wireOp",EDGE,"E16"),sQuery(id+"F0.wireOp",EDGE,"E17")])]});
            deleteBodies(context, id + "F35", {"entities" : qUnion([Q0, Q1, Q2])});
        }
        {
            var Q0;
            Q0=qCreatedBy(makeId("Right.planeOp"),FACE);
            var sketch = newSketch(context, id + "F36", { "sketchPlane" : qUnion([Q0])});
            skLineSegment(sketch, "E88", {"start": v(0, 0) * mm, "end": v(-78.77, 0) * mm});
            skSolve(sketch);
        }
        {
            var Q0;
            Q0=makeQuery(id+"F29.opExtrude","SWEPT_BODY",BODY,{"disambiguationData":[OSD([sQuery(id+"F28.wireOp",EDGE,"E59"),sQuery(id+"F28.wireOp",EDGE,"E61"),sQuery(id+"F28.wireOp",EDGE,"E58"),sQuery(id+"F28.wireOp",EDGE,"E63"),sQuery(id+"F28.wireOp",EDGE,"E64"),sQuery(id+"F28.wireOp",EDGE,"E65"),sQuery(id+"F28.wireOp",EDGE,"E66"),sQuery(id+"F28.wireOp",EDGE,"E67"),sQuery(id+"F28.wireOp",EDGE,"E69"),sQuery(id+"F28.wireOp",EDGE,"E70"),sQuery(id+"F28.wireOp",EDGE,"E71"),sQuery(id+"F28.wireOp",EDGE,"E72"),sQuery(id+"F28.wireOp",EDGE,"E73"),sQuery(id+"F28.wireOp",EDGE,"E74"),sQuery(id+"F28.wireOp",EDGE,"E75"),sQuery(id+"F28.wireOp",EDGE,"E76"),sQuery(id+"F28.wireOp",EDGE,"E77"),sQuery(id+"F28.wireOp",EDGE,"E80"),sQuery(id+"F28.wireOp",EDGE,"E81"),sQuery(id+"F28.wireOp",EDGE,"E82")])]});
            var Q1;
            Q1=sQuery(id+"F36.wireOp",EDGE,"E88");
            transform(context, id + "F37", {"entities" : qUnion([Q0]), "transformType" : TransformType.ROTATION, "transformAxis" : qUnion([Q1]), "angle" : 90 * degree, "makeCopy" : false});
        }
        {
            var Q0;
            Q0=makeQuery(id+"F29.opExtrude","SWEPT_BODY",BODY,{"disambiguationData":[OSD([sQuery(id+"F28.wireOp",EDGE,"E59"),sQuery(id+"F28.wireOp",EDGE,"E61"),sQuery(id+"F28.wireOp",EDGE,"E58"),sQuery(id+"F28.wireOp",EDGE,"E63"),sQuery(id+"F28.wireOp",EDGE,"E64"),sQuery(id+"F28.wireOp",EDGE,"E65"),sQuery(id+"F28.wireOp",EDGE,"E66"),sQuery(id+"F28.wireOp",EDGE,"E67"),sQuery(id+"F28.wireOp",EDGE,"E69"),sQuery(id+"F28.wireOp",EDGE,"E70"),sQuery(id+"F28.wireOp",EDGE,"E71"),sQuery(id+"F28.wireOp",EDGE,"E72"),sQuery(id+"F28.wireOp",EDGE,"E73"),sQuery(id+"F28.wireOp",EDGE,"E74"),sQuery(id+"F28.wireOp",EDGE,"E75"),sQuery(id+"F28.wireOp",EDGE,"E76"),sQuery(id+"F28.wireOp",EDGE,"E77"),sQuery(id+"F28.wireOp",EDGE,"E80"),sQuery(id+"F28.wireOp",EDGE,"E81"),sQuery(id+"F28.wireOp",EDGE,"E82")])]});
            transform(context, id + "F38", {"entities" : qUnion([Q0]), "transformType" : TransformType.TRANSLATION_3D, "dx" : 120 * mm, "dy" : -60 * mm, "dz" : 0 * mm, "makeCopy" : false});
        }
        {
            var Q0;
            Q0=makeQuery(id+"F29.opExtrude","SWEPT_BODY",BODY,{"disambiguationData":[OSD([sQuery(id+"F28.wireOp",EDGE,"E59"),sQuery(id+"F28.wireOp",EDGE,"E61"),sQuery(id+"F28.wireOp",EDGE,"E58"),sQuery(id+"F28.wireOp",EDGE,"E63"),sQuery(id+"F28.wireOp",EDGE,"E64"),sQuery(id+"F28.wireOp",EDGE,"E65"),sQuery(id+"F28.wireOp",EDGE,"E66"),sQuery(id+"F28.wireOp",EDGE,"E67"),sQuery(id+"F28.wireOp",EDGE,"E69"),sQuery(id+"F28.wireOp",EDGE,"E70"),sQuery(id+"F28.wireOp",EDGE,"E71"),sQuery(id+"F28.wireOp",EDGE,"E72"),sQuery(id+"F28.wireOp",EDGE,"E73"),sQuery(id+"F28.wireOp",EDGE,"E74"),sQuery(id+"F28.wireOp",EDGE,"E75"),sQuery(id+"F28.wireOp",EDGE,"E76"),sQuery(id+"F28.wireOp",EDGE,"E77"),sQuery(id+"F28.wireOp",EDGE,"E80"),sQuery(id+"F28.wireOp",EDGE,"E81"),sQuery(id+"F28.wireOp",EDGE,"E82")])]});
            var Q1;
            Q1=qCreatedBy(makeId("Right.planeOp"),FACE);
            mirror(context, id + "F39", {"entities" : qUnion([Q0]), "mirrorPlane" : qUnion([Q1])});
        }
        {
            var Q0;
            Q0=qCreatedBy(makeId("Top.planeOp"),FACE);
            var sketch = newSketch(context, id + "F40", { "sketchPlane" : qUnion([Q0])});
            skLineSegment(sketch, "E89", {"start": v(30, 25) * mm, "end": v(30, 15) * mm});
            skLineSegment(sketch, "E90", {"start": v(30, 15) * mm, "end": v(-30, 15) * mm});
            skLineSegment(sketch, "E91", {"start": v(-30, 15) * mm, "end": v(-30, 25) * mm});
            skLineSegment(sketch, "E92", {"start": v(-30, 25) * mm, "end": v(30, 25) * mm});
            skCircle(sketch, "E93", {"center": v(-25, 20) * mm, "radius": 2 * mm});
            skCircle(sketch, "E94", {"center": v(-10, 20) * mm, "radius": 2 * mm});
            skCircle(sketch, "E95", {"center": v(10, 20) * mm, "radius": 2 * mm});
            skCircle(sketch, "E96", {"center": v(25, 20) * mm, "radius": 2 * mm});
            skPoint(sketch, "E97.end.orphan", {"position": v(-30, 20) * mm});
            skSolve(sketch);
        }
        {
            var Q0;
            Q0 = qSketchRegion(id + "F40", true);
            extrude(context, id + "F41", {"entities" : qUnion([Q0]), "depth" : 8 * mm});
        }
        {
            var Q0;
            Q0=makeQuery(id+"F41.opExtrude","SWEPT_BODY",BODY,{"disambiguationData":[OSD([sQuery(id+"F40.wireOp",EDGE,"E89"),sQuery(id+"F40.wireOp",EDGE,"E90"),sQuery(id+"F40.wireOp",EDGE,"E91"),sQuery(id+"F40.wireOp",EDGE,"E92"),sQuery(id+"F40.wireOp",EDGE,"E93"),sQuery(id+"F40.wireOp",EDGE,"E94"),sQuery(id+"F40.wireOp",EDGE,"E95"),sQuery(id+"F40.wireOp",EDGE,"E96")])]});
            transform(context, id + "F42", {"entities" : qUnion([Q0]), "transformType" : TransformType.TRANSLATION_3D, "dx" : 0 * mm, "dy" : 0 * mm, "dz" : 8 * mm, "makeCopy" : false});
        }
        {
            var Q0;
            Q0=makeQuery(id+"F41.opExtrude","CAP_EDGE",EDGE,{"disambiguationData":[OSD([sQuery(id+"F40.wireOp",EDGE,"E90")])],"isStart":false});
            var Q1;
            Q1=makeQuery(id+"F41.opExtrude","SWEPT_EDGE",EDGE,{"disambiguationData":[OSD([sQuery(id+"F40.wireOp",EDGE,"E89"),sQuery(id+"F40.wireOp",EDGE,"E90")])]});
            var Q2;
            Q2=makeQuery(id+"F41.opExtrude","SWEPT_EDGE",EDGE,{"disambiguationData":[OSD([sQuery(id+"F40.wireOp",EDGE,"E89"),sQuery(id+"F40.wireOp",EDGE,"E92")])]});
            var Q3;
            Q3=makeQuery(id+"F41.opExtrude","CAP_EDGE",EDGE,{"disambiguationData":[OSD([sQuery(id+"F40.wireOp",EDGE,"E89")])],"isStart":false});
            var Q4;
            Q4=makeQuery(id+"F41.opExtrude","CAP_EDGE",EDGE,{"disambiguationData":[OSD([sQuery(id+"F40.wireOp",EDGE,"E91")])],"isStart":false});
            var Q5;
            Q5=makeQuery(id+"F41.opExtrude","SWEPT_EDGE",EDGE,{"disambiguationData":[OSD([sQuery(id+"F40.wireOp",EDGE,"E90"),sQuery(id+"F40.wireOp",EDGE,"E91")])]});
            var Q6;
            Q6=makeQuery(id+"F41.opExtrude","SWEPT_EDGE",EDGE,{"disambiguationData":[OSD([sQuery(id+"F40.wireOp",EDGE,"E91"),sQuery(id+"F40.wireOp",EDGE,"E92")])]});
            var Q7;
            Q7=makeQuery(id+"F41.opExtrude","CAP_EDGE",EDGE,{"disambiguationData":[OSD([sQuery(id+"F40.wireOp",EDGE,"E92")])],"isStart":false});
            fillet(context, id + "F43", {"entities" : qUnion([Q0, Q1, Q2, Q3, Q4, Q5, Q6, Q7]), "radius" : 1.5 * mm, "tangentPropagation" : true, "allowEdgeOverflow" : false});
        }
        {
            var Q0;
            Q0=makeQuery(id+"F39.opPattern","COPY",BODY,{"derivedFrom":makeQuery(id+"F29.opExtrude","SWEPT_BODY",BODY,{"disambiguationData":[OSD([sQuery(id+"F28.wireOp",EDGE,"E59"),sQuery(id+"F28.wireOp",EDGE,"E61"),sQuery(id+"F28.wireOp",EDGE,"E58"),sQuery(id+"F28.wireOp",EDGE,"E63"),sQuery(id+"F28.wireOp",EDGE,"E64"),sQuery(id+"F28.wireOp",EDGE,"E65"),sQuery(id+"F28.wireOp",EDGE,"E66"),sQuery(id+"F28.wireOp",EDGE,"E67"),sQuery(id+"F28.wireOp",EDGE,"E69"),sQuery(id+"F28.wireOp",EDGE,"E70"),sQuery(id+"F28.wireOp",EDGE,"E71"),sQuery(id+"F28.wireOp",EDGE,"E72"),sQuery(id+"F28.wireOp",EDGE,"E73"),sQuery(id+"F28.wireOp",EDGE,"E74"),sQuery(id+"F28.wireOp",EDGE,"E75"),sQuery(id+"F28.wireOp",EDGE,"E76"),sQuery(id+"F28.wireOp",EDGE,"E77"),sQuery(id+"F28.wireOp",EDGE,"E80"),sQuery(id+"F28.wireOp",EDGE,"E81"),sQuery(id+"F28.wireOp",EDGE,"E82")])]}),"instanceName":"1"});
            var Q1;
            Q1=makeQuery(id+"F29.opExtrude","SWEPT_BODY",BODY,{"disambiguationData":[OSD([sQuery(id+"F28.wireOp",EDGE,"E59"),sQuery(id+"F28.wireOp",EDGE,"E61"),sQuery(id+"F28.wireOp",EDGE,"E58"),sQuery(id+"F28.wireOp",EDGE,"E63"),sQuery(id+"F28.wireOp",EDGE,"E64"),sQuery(id+"F28.wireOp",EDGE,"E65"),sQuery(id+"F28.wireOp",EDGE,"E66"),sQuery(id+"F28.wireOp",EDGE,"E67"),sQuery(id+"F28.wireOp",EDGE,"E69"),sQuery(id+"F28.wireOp",EDGE,"E70"),sQuery(id+"F28.wireOp",EDGE,"E71"),sQuery(id+"F28.wireOp",EDGE,"E72"),sQuery(id+"F28.wireOp",EDGE,"E73"),sQuery(id+"F28.wireOp",EDGE,"E74"),sQuery(id+"F28.wireOp",EDGE,"E75"),sQuery(id+"F28.wireOp",EDGE,"E76"),sQuery(id+"F28.wireOp",EDGE,"E77"),sQuery(id+"F28.wireOp",EDGE,"E80"),sQuery(id+"F28.wireOp",EDGE,"E81"),sQuery(id+"F28.wireOp",EDGE,"E82")])]});
            deleteBodies(context, id + "F44", {"entities" : qUnion([Q0, Q1])});
        }
    });
